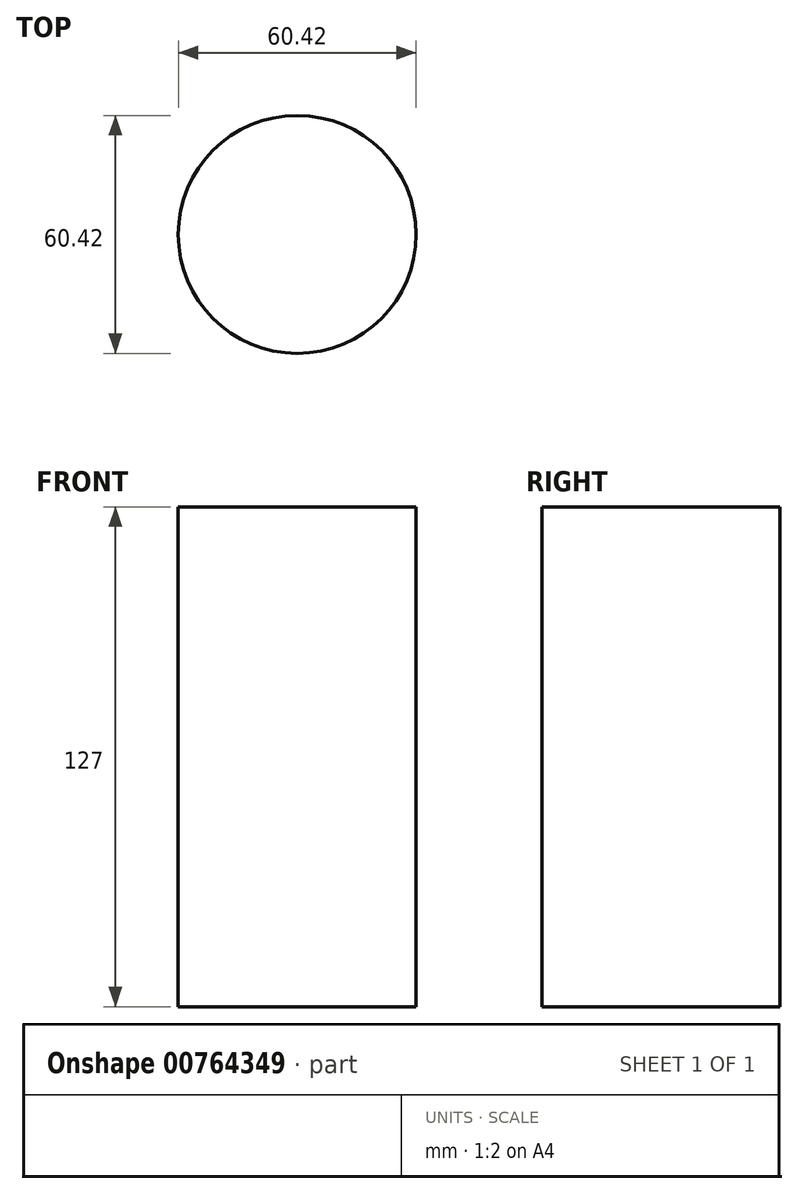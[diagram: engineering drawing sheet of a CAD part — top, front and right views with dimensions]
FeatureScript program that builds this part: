
annotation { "Feature Type Name" : "Feature", "Feature Type Description" : "" }
export const myFeature = defineFeature(function(context is Context, id is Id, definition is map)
    precondition{}
    {
        {
            var Q0;
            Q0=qCreatedBy(makeId("Top.planeOp"),FACE);
            var sketch = newSketch(context, id + "F0", { "sketchPlane" : qUnion([Q0])});
            skCircle(sketch, "E0", {"center": v(-31.94, 29.27) * mm, "radius": 30.21 * mm});
            skSolve(sketch);
        }
        {
            var Q0;
            Q0=makeQuery(id+"F0.imprint","IMPRINT",FACE,{"disambiguationData":[TD([[makeQuery(id+"F0.imprint","IMPRINT",EDGE,{"derivedFrom":sQuery(id+"F0.wireOp",EDGE,"E0")}),1.0]])]});
            extrude(context, id + "F1", {"entities" : qUnion([Q0]), "depth" : 127 * mm, "offsetDistance" : 25.4 * mm});
        }
    });
